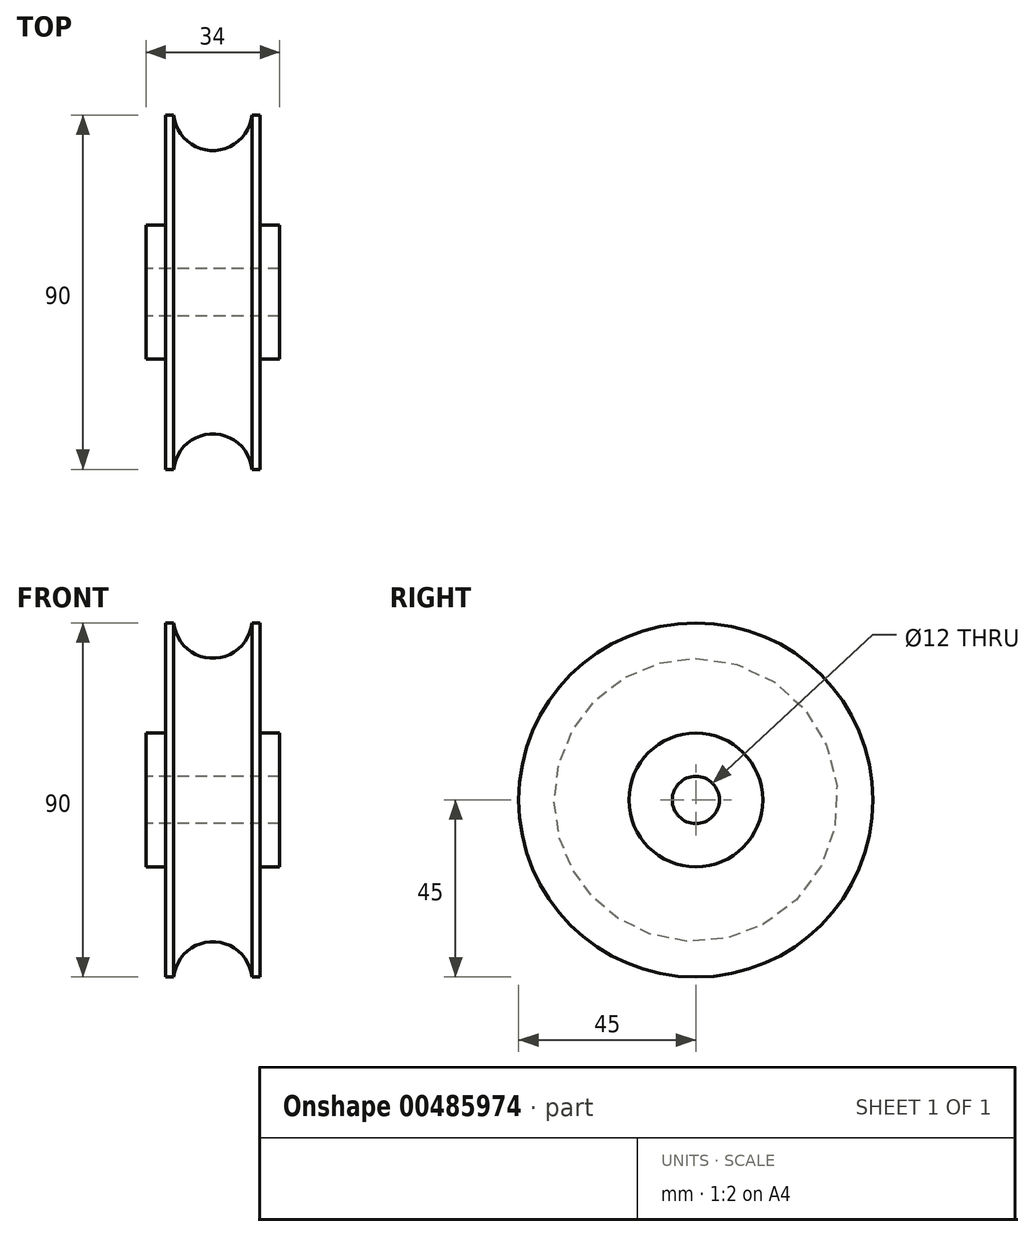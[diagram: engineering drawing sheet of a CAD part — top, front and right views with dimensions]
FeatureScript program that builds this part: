
annotation { "Feature Type Name" : "Feature", "Feature Type Description" : "" }
export const myFeature = defineFeature(function(context is Context, id is Id, definition is map)
    precondition{}
    {
        {
            var Q0;
            Q0=qCreatedBy(makeId("Top.planeOp"),FACE);
            var sketch = newSketch(context, id + "F0", { "sketchPlane" : qUnion([Q0])});
            skLineSegment(sketch, "E0", {"start": v(0, 47.97) * mm, "end": v(0, -45.27) * mm, "construction": true});
            skLineSegment(sketch, "E1", {"start": v(-40.81, 0) * mm, "end": v(48.24, 0) * mm, "construction": true});
            skLineSegment(sketch, "E2", {"start": v(-17, 6) * mm, "end": v(0, 6) * mm});
            skLineSegment(sketch, "E3", {"start": v(-17, 6) * mm, "end": v(-17, 17) * mm});
            skLineSegment(sketch, "E4", {"start": v(-17, 17) * mm, "end": v(-12, 17) * mm});
            skLineSegment(sketch, "E5", {"start": v(-12, 17) * mm, "end": v(-12, 45) * mm});
            skLineSegment(sketch, "E6.MirrorCS", {"start": v(12, 17) * mm, "end": v(12, 45) * mm});
            skLineSegment(sketch, "E7.MirrorCS", {"start": v(17, 6) * mm, "end": v(0, 6) * mm});
            skLineSegment(sketch, "E8.MirrorCS", {"start": v(17, 6) * mm, "end": v(17, 17) * mm});
            skLineSegment(sketch, "E9.MirrorCS", {"start": v(17, 17) * mm, "end": v(12, 17) * mm});
            skArc(sketch, "E10", {"start": v(-9.95, 45) * mm, "mid": v(0, 36) * mm, "end": v(9.95, 45) * mm});
            skLineSegment(sketch, "E11", {"start": v(-12, 45) * mm, "end": v(-9.95, 45) * mm});
            skLineSegment(sketch, "E12.trimOffspring", {"start": v(9.95, 45) * mm, "end": v(12, 45) * mm});
            skSolve(sketch);
        }
        {
            var Q0;
            Q0=makeQuery(id+"F0.imprint","IMPRINT",FACE,{"disambiguationData":[TD([[makeQuery(id+"F0.imprint","IMPRINT",EDGE,{"derivedFrom":sQuery(id+"F0.wireOp",EDGE,"E2")}),1.0]])]});
            var Q1;
            Q1=sQuery(id+"F0.wireOp",EDGE,"E1");
            revolve(context, id + "F1", {"entities" : qUnion([Q0]), "axis" : qUnion([Q1]), "revolveType" : RevolveType.FULL});
        }
    });
